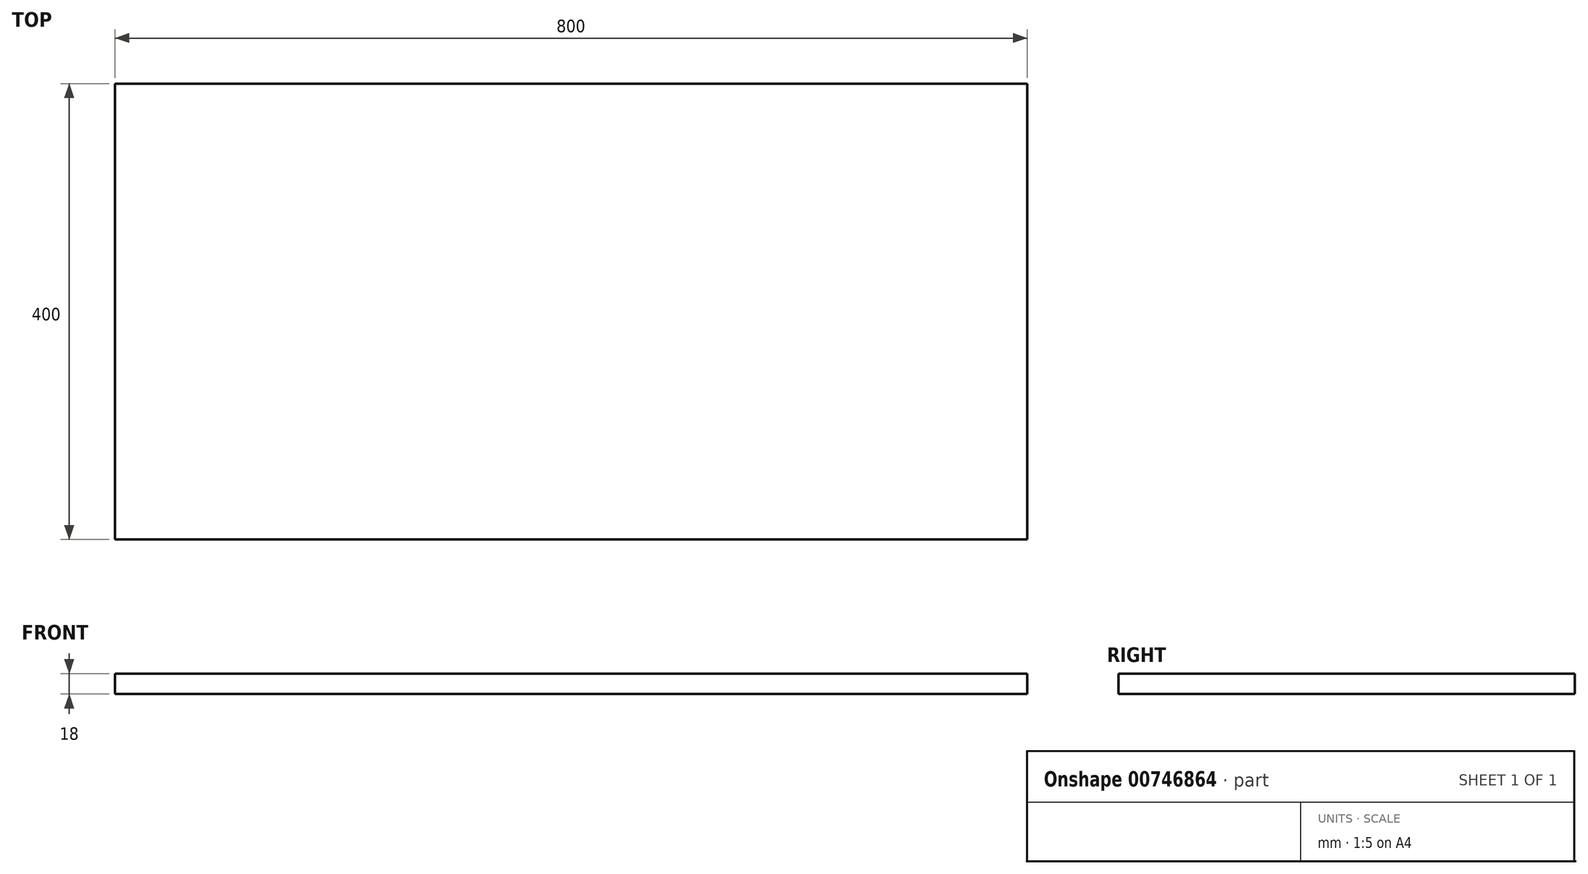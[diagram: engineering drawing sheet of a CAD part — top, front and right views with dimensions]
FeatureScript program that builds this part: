
annotation { "Feature Type Name" : "Feature", "Feature Type Description" : "" }
export const myFeature = defineFeature(function(context is Context, id is Id, definition is map)
    precondition{}
    {
        {
            var Q0;
            Q0=qCreatedBy(makeId("Top.planeOp"),FACE);
            var sketch = newSketch(context, id + "F0", { "sketchPlane" : qUnion([Q0])});
            skLineSegment(sketch, "E0.bottom", {"start": v(-400, 200) * mm, "end": v(400, 200) * mm});
            skLineSegment(sketch, "E0.top", {"start": v(-400, -200) * mm, "end": v(400, -200) * mm});
            skLineSegment(sketch, "E0.left", {"start": v(-400, 200) * mm, "end": v(-400, -200) * mm});
            skLineSegment(sketch, "E0.right", {"start": v(400, 200) * mm, "end": v(400, -200) * mm});
            skPoint(sketch, "E0.middle", {"position": v(0, 0) * mm});
            skSolve(sketch);
        }
        {
            var Q0;
            Q0=makeQuery(id+"F0.imprint","IMPRINT",FACE,{"disambiguationData":[TD([[makeQuery(id+"F0.imprint","IMPRINT",EDGE,{"derivedFrom":sQuery(id+"F0.wireOp",EDGE,"E0.bottom")}),-1.0]])]});
            extrude(context, id + "F1", {"entities" : qUnion([Q0]), "depth" : 18 * mm, "offsetDistance" : 25 * mm});
        }
    });
